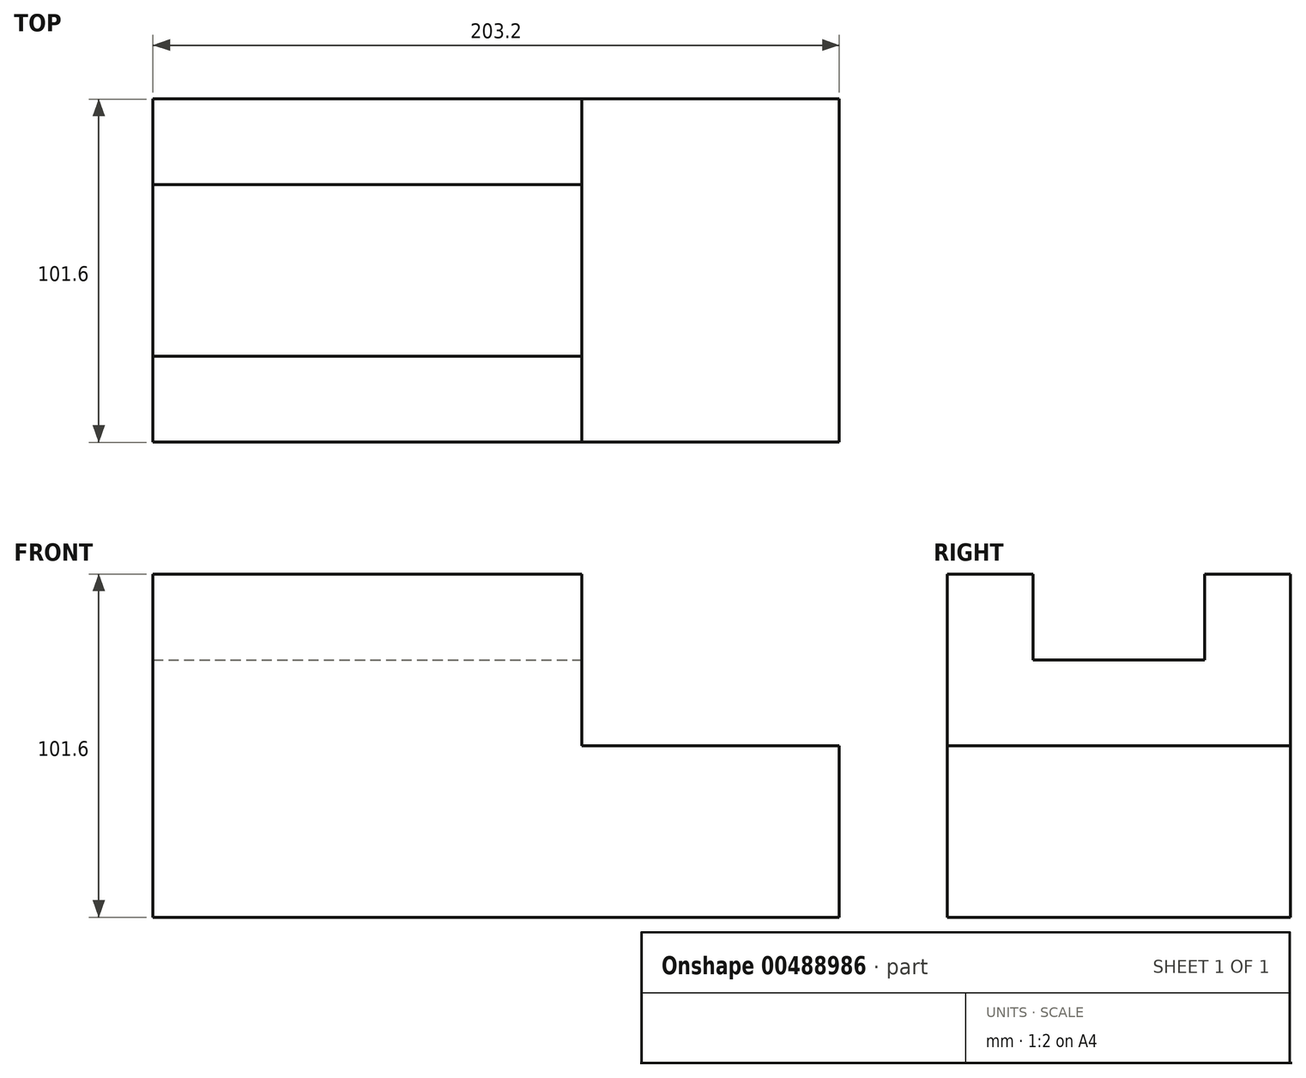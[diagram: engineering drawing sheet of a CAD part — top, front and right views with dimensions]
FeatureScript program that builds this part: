
annotation { "Feature Type Name" : "Feature", "Feature Type Description" : "" }
export const myFeature = defineFeature(function(context is Context, id is Id, definition is map)
    precondition{}
    {
        {
            var Q0;
            Q0=qCreatedBy(makeId("Top.planeOp"),FACE);
            var sketch = newSketch(context, id + "F0", { "sketchPlane" : qUnion([Q0])});
            skLineSegment(sketch, "E0.bottom", {"start": v(116.38, -55.2) * mm, "end": v(-86.82, -55.2) * mm});
            skLineSegment(sketch, "E0.top", {"start": v(116.38, 46.4) * mm, "end": v(-86.82, 46.4) * mm});
            skLineSegment(sketch, "E0.left", {"start": v(116.38, -55.2) * mm, "end": v(116.38, 46.4) * mm});
            skLineSegment(sketch, "E0.right", {"start": v(-86.82, -55.2) * mm, "end": v(-86.82, 46.4) * mm});
            skSolve(sketch);
        }
        {
            var Q0;
            Q0 = qSketchRegion(id + "F0", true);
            extrude(context, id + "F1", {"entities" : qUnion([Q0]), "depth" : 50.8 * mm});
        }
        {
            var Q0;
            Q0=makeQuery(id+"F1.opExtrude","SWEPT_FACE",FACE,{"disambiguationData":[OSD([sQuery(id+"F0.wireOp",EDGE,"E0.bottom")])]});
            var sketch = newSketch(context, id + "F2", { "sketchPlane" : qUnion([Q0])});
            skLineSegment(sketch, "E1.bottom", {"start": v(-86.82, 50.8) * mm, "end": v(40.18, 50.8) * mm});
            skLineSegment(sketch, "E1.top", {"start": v(-86.82, 101.6) * mm, "end": v(40.18, 101.6) * mm});
            skLineSegment(sketch, "E1.left", {"start": v(-86.82, 50.8) * mm, "end": v(-86.82, 101.6) * mm});
            skLineSegment(sketch, "E1.right", {"start": v(40.18, 50.8) * mm, "end": v(40.18, 101.6) * mm});
            skSolve(sketch);
        }
        {
            var Q0;
            Q0=makeQuery(id+"F2.imprint","IMPRINT",FACE,{"disambiguationData":[TD([[makeQuery(id+"F2.imprint","IMPRINT",EDGE,{"derivedFrom":sQuery(id+"F2.wireOp",EDGE,"E1.bottom")}),-1.0]])]});
            extrude(context, id + "F3", {"entities" : qUnion([Q0]), "operationType" : NewBodyOperationType.ADD, "depth" : -101.6 * mm});
        }
        {
            var Q0;
            Q0=makeQuery(id+"F3.opExtrude","SWEPT_FACE",FACE,{"disambiguationData":[OSD([sQuery(id+"F2.wireOp",EDGE,"E1.right")])]});
            var sketch = newSketch(context, id + "F4", { "sketchPlane" : qUnion([Q0])});
            skLineSegment(sketch, "E2.bottom", {"start": v(-29.8, 101.6) * mm, "end": v(21, 101.6) * mm});
            skLineSegment(sketch, "E2.top", {"start": v(-29.8, 76.2) * mm, "end": v(21, 76.2) * mm});
            skLineSegment(sketch, "E2.left", {"start": v(-29.8, 101.6) * mm, "end": v(-29.8, 76.2) * mm});
            skLineSegment(sketch, "E2.right", {"start": v(21, 101.6) * mm, "end": v(21, 76.2) * mm});
            skSolve(sketch);
        }
        {
            var Q0;
            Q0 = qSketchRegion(id + "F4", true);
            extrude(context, id + "F5", {"entities" : qUnion([Q0]), "operationType" : NewBodyOperationType.REMOVE, "endBound" : BoundingType.THROUGH_ALL, "oppositeDirection" : true, "depth" : 25.4 * mm});
        }
    });
